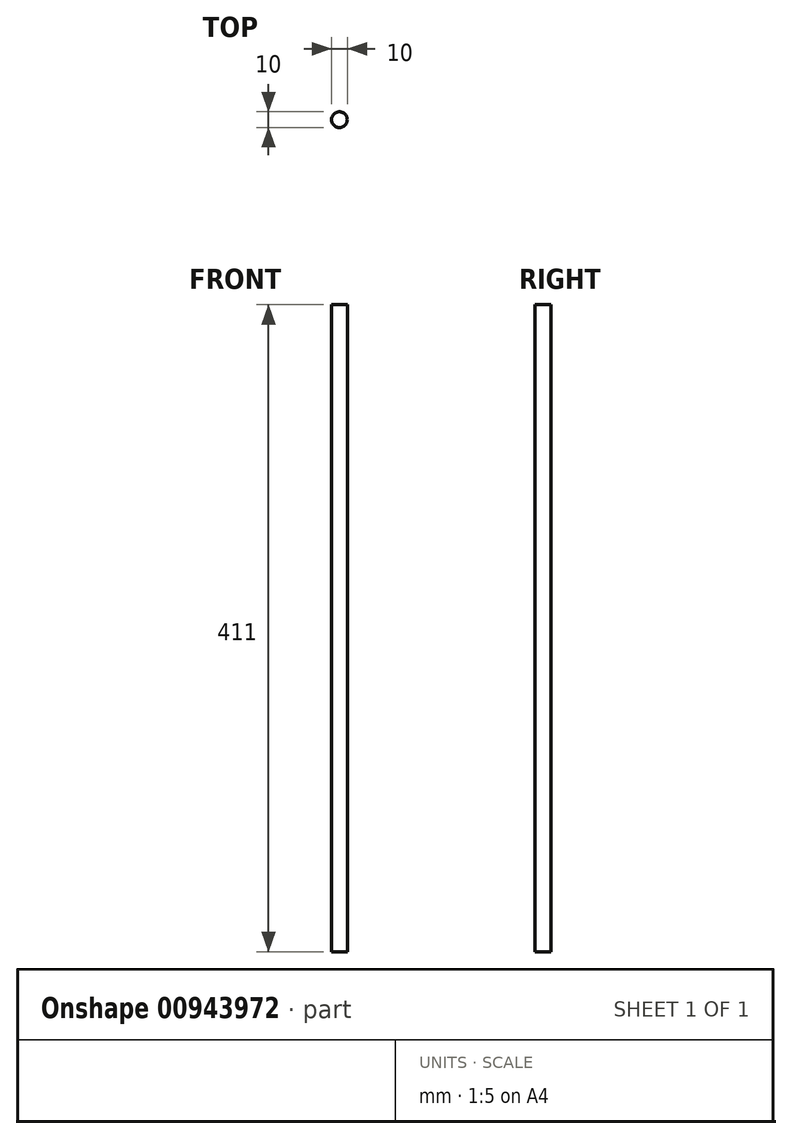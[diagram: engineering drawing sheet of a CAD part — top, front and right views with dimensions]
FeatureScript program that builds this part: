
annotation { "Feature Type Name" : "Feature", "Feature Type Description" : "" }
export const myFeature = defineFeature(function(context is Context, id is Id, definition is map)
    precondition{}
    {
        {
            var Q0;
            Q0=qCreatedBy(makeId("Top.planeOp"),FACE);
            var sketch = newSketch(context, id + "F0", { "sketchPlane" : qUnion([Q0])});
            skCircle(sketch, "E0", {"center": v(0, 0) * mm, "radius": 5 * mm});
            skSolve(sketch);
        }
        {
            var Q0;
            Q0=makeQuery(id+"F0.imprint","IMPRINT",FACE,{"disambiguationData":[TD([[makeQuery(id+"F0.imprint","IMPRINT",EDGE,{"derivedFrom":sQuery(id+"F0.wireOp",EDGE,"E0")}),1.0]])]});
            extrude(context, id + "F1", {"entities" : qUnion([Q0]), "flatOperationType" : FlatOperationType.REMOVE, "depth" : 411 * mm, "offsetDistance" : 25 * mm, "domain" : OperationDomain.MODEL});
        }
    });
